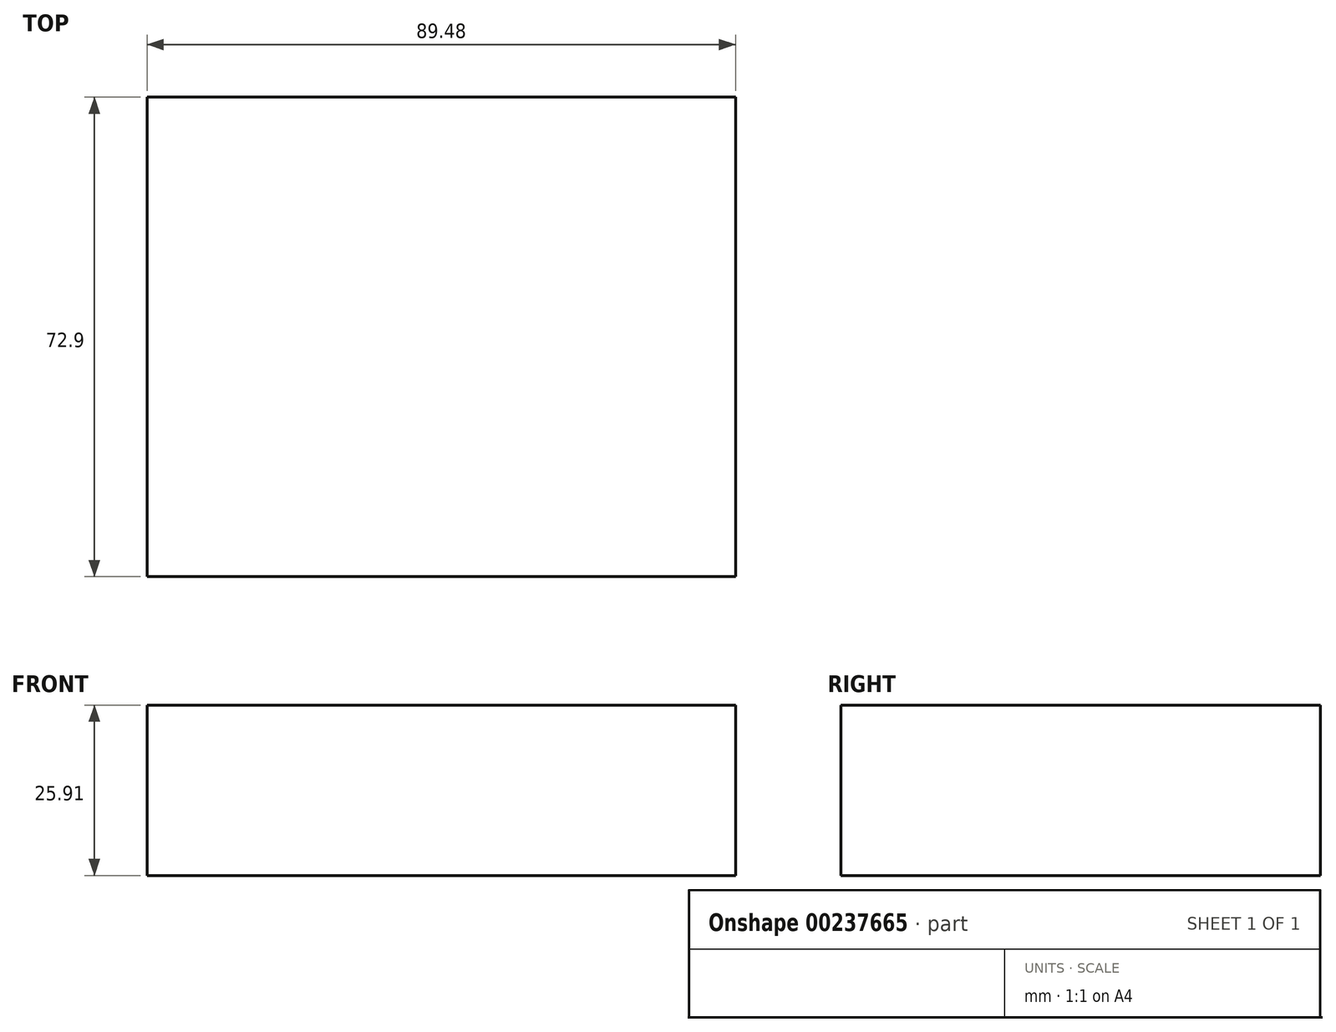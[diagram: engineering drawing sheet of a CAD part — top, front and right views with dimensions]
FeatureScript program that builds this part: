
annotation { "Feature Type Name" : "Feature", "Feature Type Description" : "" }
export const myFeature = defineFeature(function(context is Context, id is Id, definition is map)
    precondition{}
    {
        {
            var Q0;
            Q0=qCreatedBy(makeId("Front.planeOp"),FACE);
            var sketch = newSketch(context, id + "F0", { "sketchPlane" : qUnion([Q0])});
            skLineSegment(sketch, "E0.bottom", {"start": v(0, 0) * mm, "end": v(-89.48, 0) * mm});
            skLineSegment(sketch, "E0.top", {"start": v(0, -25.9) * mm, "end": v(-89.48, -25.9) * mm});
            skLineSegment(sketch, "E0.left", {"start": v(0, 0) * mm, "end": v(0, -25.9) * mm});
            skLineSegment(sketch, "E0.right", {"start": v(-89.48, 0) * mm, "end": v(-89.48, -25.9) * mm});
            skSolve(sketch);
        }
        {
            var Q0;
            Q0=makeQuery(id+"F0.imprint","IMPRINT",FACE,{"disambiguationData":[TD([[makeQuery(id+"F0.imprint","IMPRINT",EDGE,{"derivedFrom":sQuery(id+"F0.wireOp",EDGE,"E0.bottom")}),1.0]])]});
            extrude(context, id + "F1", {"entities" : qUnion([Q0]), "depth" : 72.9 * mm});
        }
    });
